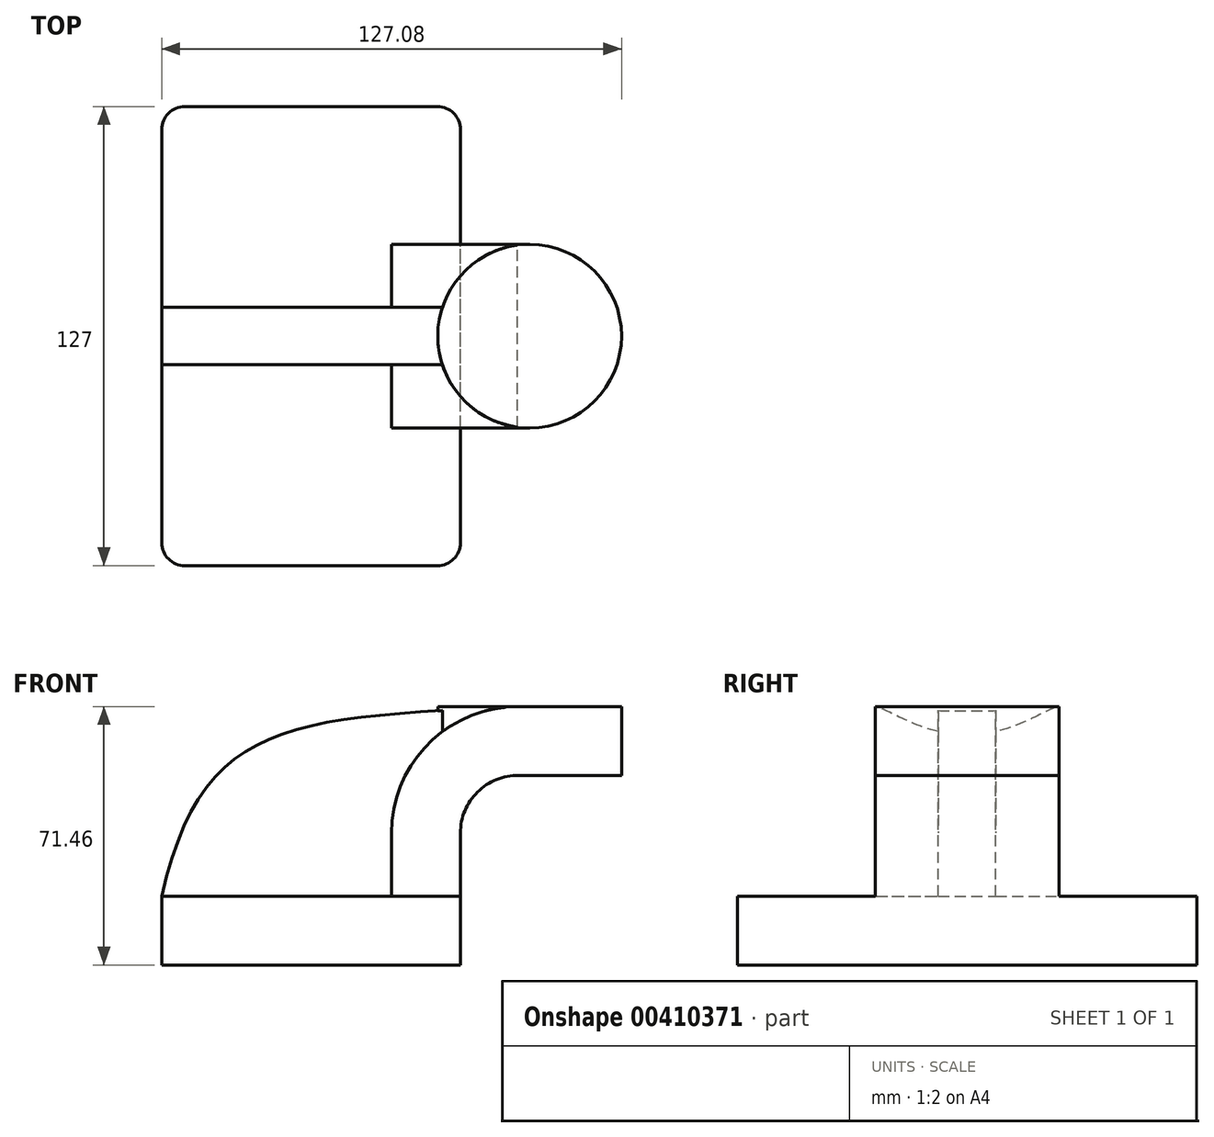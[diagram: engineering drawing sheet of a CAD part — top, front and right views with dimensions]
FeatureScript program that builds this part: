
annotation { "Feature Type Name" : "Feature", "Feature Type Description" : "" }
export const myFeature = defineFeature(function(context is Context, id is Id, definition is map)
    precondition{}
    {
        {
            var Q0;
            Q0=qCreatedBy(makeId("Front.planeOp"),FACE);
            var sketch = newSketch(context, id + "F0", { "sketchPlane" : qUnion([Q0])});
            skLineSegment(sketch, "E0.bottom", {"start": v(41.28, -9.53) * mm, "end": v(-41.28, -9.53) * mm});
            skLineSegment(sketch, "E0.top", {"start": v(41.28, 9.53) * mm, "end": v(-41.28, 9.53) * mm});
            skLineSegment(sketch, "E0.left", {"start": v(41.28, -9.52) * mm, "end": v(41.28, 9.53) * mm});
            skLineSegment(sketch, "E0.right", {"start": v(-41.28, -9.52) * mm, "end": v(-41.28, 9.53) * mm});
            skPoint(sketch, "E0.middle", {"position": v(0, 0) * mm});
            skLineSegment(sketch, "E1.bottom", {"start": v(111.2, 38.1) * mm, "end": v(60.4, 38.1) * mm});
            skLineSegment(sketch, "E1.top", {"start": v(111.2, 66.67) * mm, "end": v(60.4, 66.67) * mm});
            skLineSegment(sketch, "E1.left", {"start": v(111.2, 38.1) * mm, "end": v(111.2, 66.68) * mm});
            skLineSegment(sketch, "E1.right", {"start": v(60.4, 38.1) * mm, "end": v(60.4, 66.68) * mm});
            skPoint(sketch, "E1.middle", {"position": v(85.8, 52.39) * mm});
            skLineSegment(sketch, "E2", {"start": v(41.28, 9.53) * mm, "end": v(41.28, 27) * mm});
            skArc(sketch, "E3", {"start": v(41.28, 27) * mm, "mid": v(46, 38.3) * mm, "end": v(57.34, 42.88) * mm});
            skLineSegment(sketch, "E4", {"start": v(57.34, 42.88) * mm, "end": v(102.71, 42.88) * mm});
            skLineSegment(sketch, "E5.0", {"start": v(56.87, 61.93) * mm, "end": v(85.8, 61.93) * mm});
            skArc(sketch, "E5.1", {"start": v(22.23, 27) * mm, "mid": v(32.36, 51.6) * mm, "end": v(56.87, 61.93) * mm});
            skLineSegment(sketch, "E5.2", {"start": v(22.22, 9.53) * mm, "end": v(22.22, 27) * mm});
            skLineSegment(sketch, "E6", {"start": v(85.8, 61.93) * mm, "end": v(85.8, 42.88) * mm});
            skPoint(sketch, "E7", {"position": v(85.8, 66.67) * mm});
            skFitSpline(sketch, "E8", {"points": [v(-41.28, 9.53) * mm, v(56.87, 61.93) * mm], "startDerivative": vector(33.1, 147.7) * mm, "endDerivative": vector(187.12, 9.51) * mm});
            skSolve(sketch);
        }
        {
            var Q0;
            {var subQ1=sQuery(id+"F0.wireOp",EDGE,"E2");Q0=makeQuery(id+"F0.imprint","IMPRINT",FACE,{"disambiguationData":[TD([[makeQuery(id+"F0.imprint","IMPRINT",EDGE,{"derivedFrom":subQ1}),1.0]])]});}
            extrude(context, id + "F1", {"entities" : qUnion([Q0]), "endBound" : BoundingType.SYMMETRIC, "depth" : 50.8 * mm});
        }
        {
            var Q0;
            Q0=makeQuery(id+"F0.imprint","IMPRINT",FACE,{"disambiguationData":[TD([[makeQuery(id+"F0.imprint","IMPRINT",EDGE,{"derivedFrom":sQuery(id+"F0.wireOp",EDGE,"E0.bottom")}),-1.0]])]});
            extrude(context, id + "F2", {"entities" : qUnion([Q0]), "operationType" : NewBodyOperationType.ADD, "endBound" : BoundingType.SYMMETRIC, "depth" : 127 * mm});
        }
        {
            var Q0;
            {var subQ3=sQuery(id+"F0.wireOp",EDGE,"E5.2");Q0=makeQuery(id+"F0.imprint","IMPRINT",FACE,{"disambiguationData":[TD([[makeQuery(id+"F0.imprint","IMPRINT",EDGE,{"derivedFrom":subQ3}),1.0]])]});}
            extrude(context, id + "F3", {"entities" : qUnion([Q0]), "operationType" : NewBodyOperationType.ADD, "endBound" : BoundingType.SYMMETRIC, "depth" : 15.88 * mm});
        }
        {
            var Q0;
            {var subQ5=sQuery(id+"F0.wireOp",EDGE,"E6");Q0=makeQuery(id+"F0.imprint","IMPRINT",FACE,{"disambiguationData":[TD([[makeQuery(id+"F0.imprint","IMPRINT",EDGE,{"derivedFrom":subQ5}),-1.0]])]});}
            var Q1;
            Q1=sQuery(id+"F0.wireOp",EDGE,"E1.right");
            revolve(context, id + "F4", {"operationType" : NewBodyOperationType.ADD, "entities" : qUnion([Q0]), "axis" : qUnion([Q1]), "revolveType" : RevolveType.FULL});
        }
        {
            var Q0;
            Q0=makeQuery(id+"F2.opExtrude","CAP_EDGE",EDGE,{"disambiguationData":[OSD([sQuery(id+"F0.wireOp",EDGE,"E0.left")])],"isStart":false});
            var Q1;
            Q1=makeQuery(id+"F2.opExtrude","CAP_EDGE",EDGE,{"disambiguationData":[OSD([sQuery(id+"F0.wireOp",EDGE,"E0.right")])],"isStart":false});
            var Q2;
            Q2=makeQuery(id+"F2.opExtrude","CAP_EDGE",EDGE,{"disambiguationData":[OSD([sQuery(id+"F0.wireOp",EDGE,"E0.left")])],"isStart":true});
            var Q3;
            Q3=makeQuery(id+"F2.opExtrude","CAP_EDGE",EDGE,{"disambiguationData":[OSD([sQuery(id+"F0.wireOp",EDGE,"E0.right")])],"isStart":true});
            fillet(context, id + "F5", {"entities" : qUnion([Q0, Q1, Q2, Q3]), "radius" : 6.35 * mm, "tangentPropagation" : true, "allowEdgeOverflow" : false});
        }
    });
